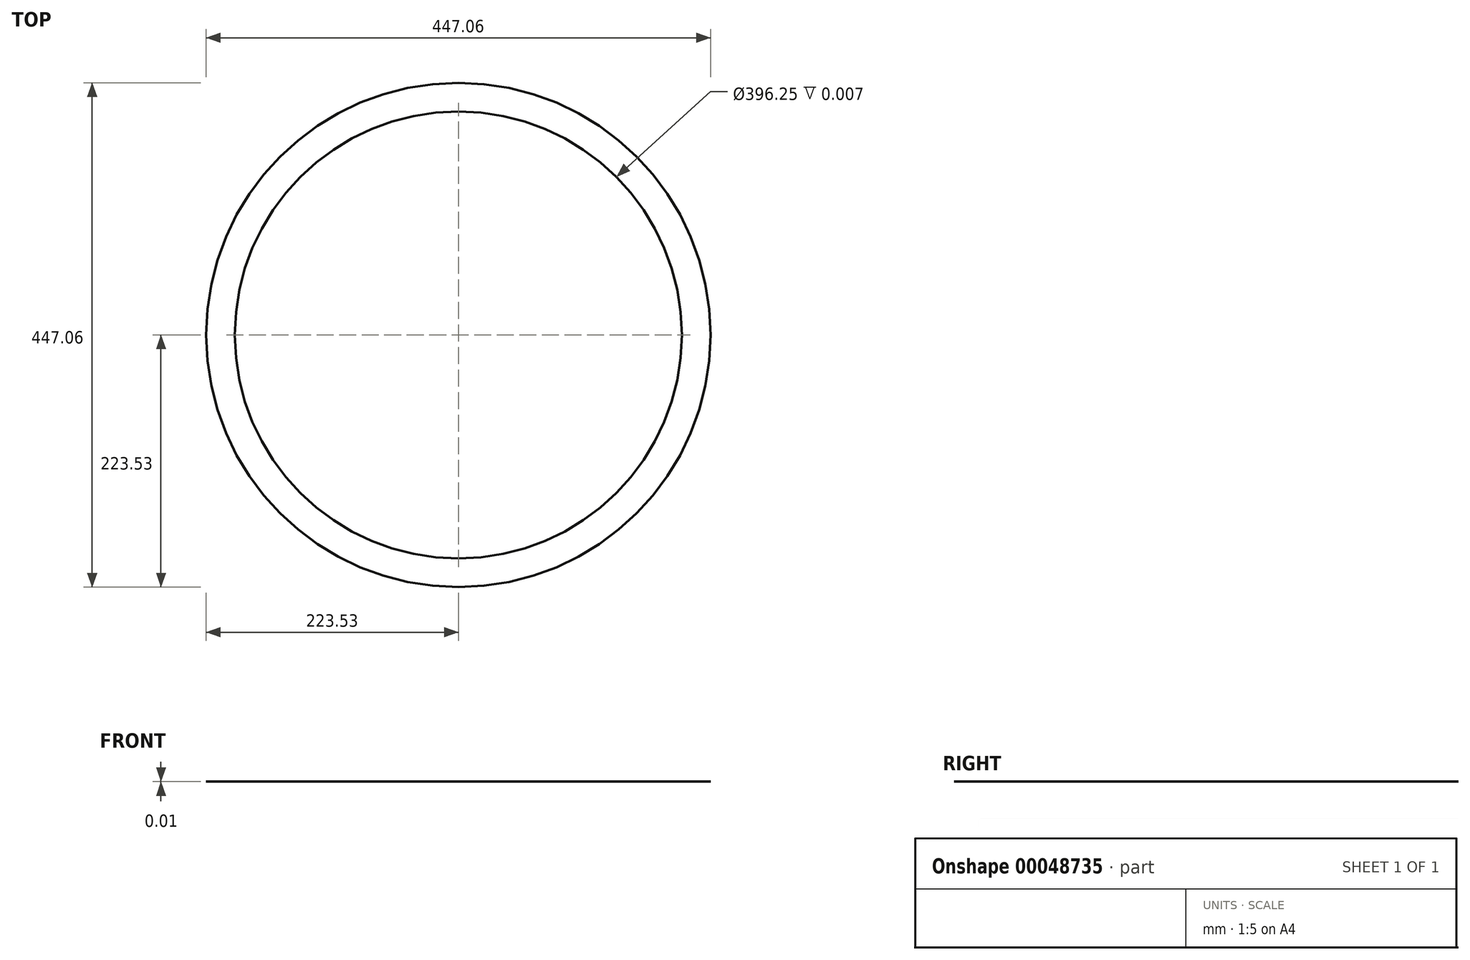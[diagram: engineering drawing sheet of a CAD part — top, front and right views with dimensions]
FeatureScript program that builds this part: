
annotation { "Feature Type Name" : "Feature", "Feature Type Description" : "" }
export const myFeature = defineFeature(function(context is Context, id is Id, definition is map)
    precondition{}
    {
        {
            var Q0;
            Q0=qCreatedBy(makeId("Top.planeOp"),FACE);
            var sketch = newSketch(context, id + "F0", { "sketchPlane" : qUnion([Q0])});
            skCircle(sketch, "E0", {"center": v(0, 0) * mm, "radius": 223.53 * mm});
            skCircle(sketch, "E1", {"center": v(0, 0) * mm, "radius": 198.13 * mm});
            skSolve(sketch);
        }
        {
            var Q0;
            Q0=makeQuery(id+"F0.imprint","IMPRINT",FACE,{"disambiguationData":[TD([[makeQuery(id+"F0.imprint","IMPRINT",EDGE,{"derivedFrom":sQuery(id+"F0.wireOp",EDGE,"E0")}),1.0]])]});
            extrude(context, id + "F1", {"entities" : qUnion([Q0]), "depth" : 3 / 406.4 * mm});
        }
    });
